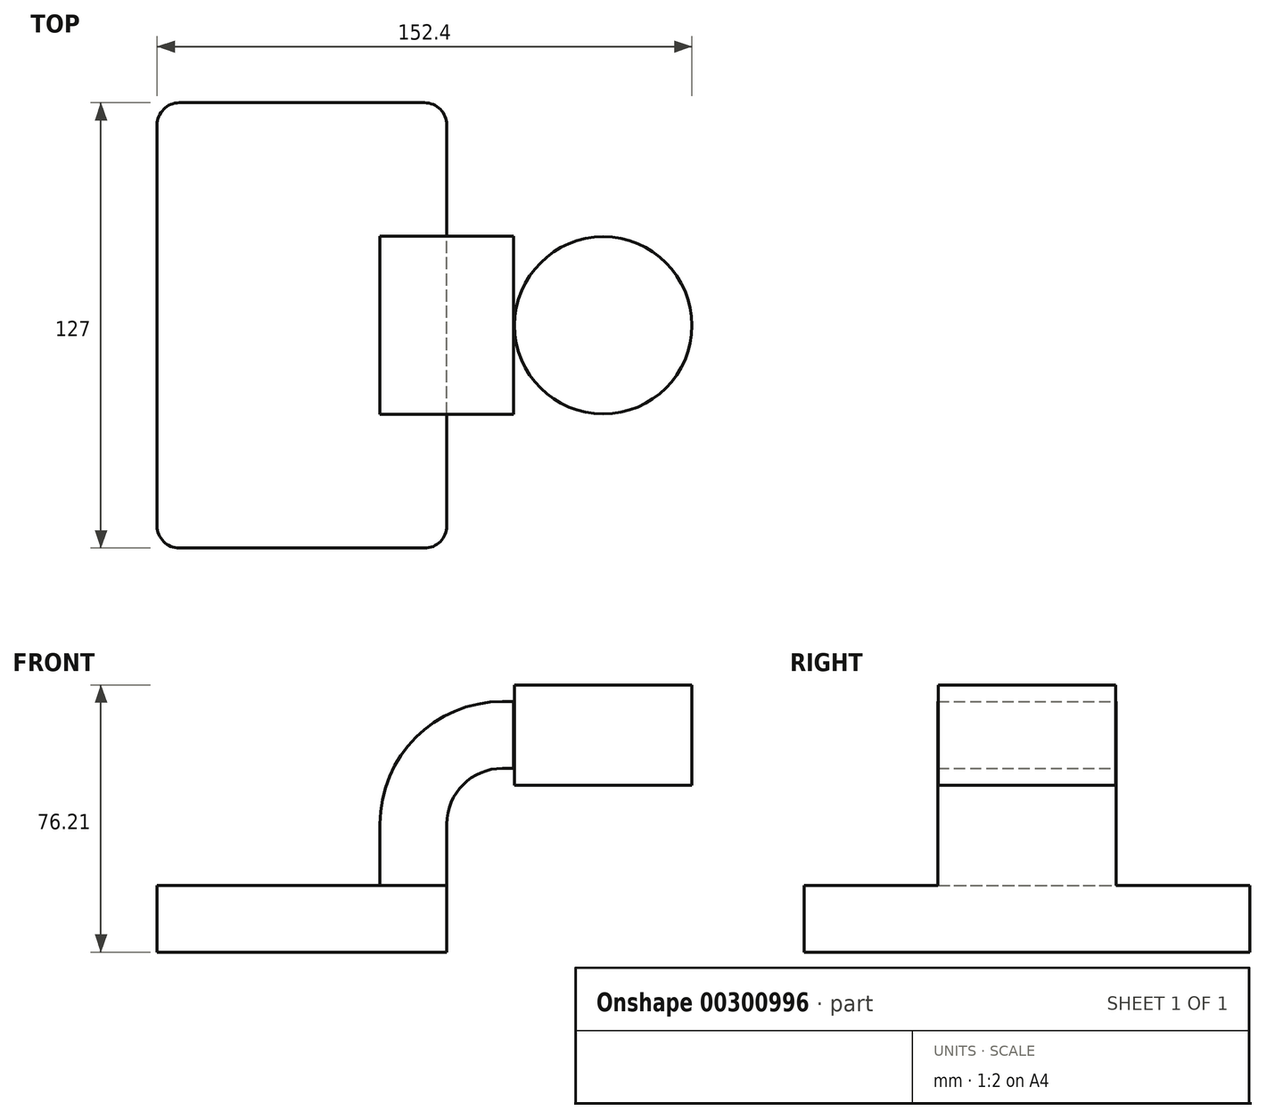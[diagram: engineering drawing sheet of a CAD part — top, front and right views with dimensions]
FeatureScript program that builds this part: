
annotation { "Feature Type Name" : "Feature", "Feature Type Description" : "" }
export const myFeature = defineFeature(function(context is Context, id is Id, definition is map)
    precondition{}
    {
        {
            var Q0;
            Q0=qCreatedBy(makeId("Front.planeOp"),FACE);
            var sketch = newSketch(context, id + "F0", { "sketchPlane" : qUnion([Q0])});
            skLineSegment(sketch, "E0.bottom", {"start": v(-41.28, 9.52) * mm, "end": v(41.27, 9.53) * mm});
            skLineSegment(sketch, "E0.top", {"start": v(-41.28, -9.53) * mm, "end": v(41.28, -9.53) * mm});
            skLineSegment(sketch, "E0.left", {"start": v(-41.28, 9.52) * mm, "end": v(-41.27, -9.53) * mm});
            skLineSegment(sketch, "E0.right", {"start": v(41.28, 9.53) * mm, "end": v(41.28, -9.52) * mm});
            skPoint(sketch, "E0.middle", {"position": v(0, 0) * mm});
            skLineSegment(sketch, "E1.bottom", {"start": v(60.32, 66.68) * mm, "end": v(111.12, 66.68) * mm});
            skLineSegment(sketch, "E1.top", {"start": v(60.32, 38.1) * mm, "end": v(111.12, 38.1) * mm});
            skLineSegment(sketch, "E1.left", {"start": v(60.32, 66.68) * mm, "end": v(60.32, 38.1) * mm});
            skLineSegment(sketch, "E1.right", {"start": v(111.12, 66.68) * mm, "end": v(111.12, 38.1) * mm});
            skPoint(sketch, "E1.middle", {"position": v(85.72, 52.39) * mm});
            skLineSegment(sketch, "E2", {"start": v(41.27, 9.53) * mm, "end": v(41.27, 27) * mm});
            skArc(sketch, "E3", {"start": v(41.27, 27) * mm, "mid": v(45.92, 38.23) * mm, "end": v(57.15, 42.88) * mm});
            skLineSegment(sketch, "E4", {"start": v(57.15, 42.88) * mm, "end": v(85.86, 42.88) * mm});
            skLineSegment(sketch, "E5.0", {"start": v(57.15, 61.93) * mm, "end": v(85.72, 61.93) * mm});
            skArc(sketch, "E5.1", {"start": v(22.22, 27) * mm, "mid": v(32.45, 51.7) * mm, "end": v(57.15, 61.93) * mm});
            skLineSegment(sketch, "E5.2", {"start": v(22.22, 9.53) * mm, "end": v(22.22, 27) * mm});
            skFitSpline(sketch, "E6", {"points": [v(-41.28, 9.52) * mm, v(57.15, 61.93) * mm], "startDerivative": vector(1, 104.21) * mm, "endDerivative": vector(115.49, -5.89) * mm});
            skLineSegment(sketch, "E7", {"start": v(85.86, 38.1) * mm, "end": v(85.86, 66.68) * mm});
            skLineSegment(sketch, "E8", {"start": v(60.32, 61.93) * mm, "end": v(60.32, 42.88) * mm});
            skLineSegment(sketch, "E9", {"start": v(60.32, 42.88) * mm, "end": v(85.86, 42.88) * mm});
            skLineSegment(sketch, "E10", {"start": v(85.72, 61.93) * mm, "end": v(85.86, 66.68) * mm});
            skLineSegment(sketch, "E11", {"start": v(60.32, 61.93) * mm, "end": v(60.32, 66.68) * mm});
            skSolve(sketch);
        }
        {
            var Q0;
            Q0=makeQuery(id+"F0.imprint","IMPRINT",FACE,{"disambiguationData":[TD([[makeQuery(id+"F0.imprint","IMPRINT",EDGE,{"derivedFrom":sQuery(id+"F0.wireOp",EDGE,"E0.top")}),1.0]])]});
            extrude(context, id + "F1", {"entities" : qUnion([Q0]), "endBound" : BoundingType.SYMMETRIC, "depth" : 127 * mm});
        }
        {
            var Q0;
            {var subQ1=sQuery(id+"F0.wireOp",EDGE,"E2");Q0=makeQuery(id+"F0.imprint","IMPRINT",FACE,{"disambiguationData":[TD([[makeQuery(id+"F0.imprint","IMPRINT",EDGE,{"derivedFrom":subQ1}),1.0]])]});}
            var Q1;
            {var subQ1=sQuery(id+"F0.wireOp",EDGE,"E8");Q1=makeQuery(id+"F0.imprint","IMPRINT",FACE,{"disambiguationData":[TD([[makeQuery(id+"F0.imprint","IMPRINT",EDGE,{"derivedFrom":subQ1}),1.0]])]});}
            extrude(context, id + "F2", {"entities" : qUnion([Q0, Q1]), "operationType" : NewBodyOperationType.ADD, "endBound" : BoundingType.SYMMETRIC, "depth" : 50.8 * mm});
        }
        {
            var Q0;
            Q0=makeQuery(id+"F0.imprint","IMPRINT",FACE,{"disambiguationData":[TD([[makeQuery(id+"F0.imprint","IMPRINT",EDGE,{"derivedFrom":sQuery(id+"F0.wireOp",EDGE,"E5.1")}),1.0]])]});
            extrude(context, id + "F3", {"entities" : qUnion([Q0]), "operationType" : NewBodyOperationType.ADD, "endBound" : BoundingType.SYMMETRIC, "depth" : 15.88 * mm});
        }
        {
            var Q0;
            {var subQ0=sQuery(id+"F0.wireOp",EDGE,"E1.right");Q0=makeQuery(id+"F0.imprint","IMPRINT",FACE,{"disambiguationData":[TD([[makeQuery(id+"F0.imprint","IMPRINT",EDGE,{"derivedFrom":subQ0}),-1.0]])]});}
            var Q1;
            Q1=sQuery(id+"F0.wireOp",EDGE,"E7");
            revolve(context, id + "F4", {"entities" : qUnion([Q0]), "axis" : qUnion([Q1]), "revolveType" : RevolveType.FULL});
        }
        {
            var Q0;
            Q0=makeQuery(id+"F1.opExtrude","CAP_EDGE",EDGE,{"disambiguationData":[OSD([sQuery(id+"F0.wireOp",EDGE,"E0.left")])],"isStart":false});
            var Q1;
            Q1=makeQuery(id+"F1.opExtrude","CAP_EDGE",EDGE,{"disambiguationData":[OSD([sQuery(id+"F0.wireOp",EDGE,"E0.right")])],"isStart":false});
            var Q2;
            Q2=makeQuery(id+"F1.opExtrude","CAP_EDGE",EDGE,{"disambiguationData":[OSD([sQuery(id+"F0.wireOp",EDGE,"E0.right")])],"isStart":true});
            var Q3;
            Q3=makeQuery(id+"F1.opExtrude","CAP_EDGE",EDGE,{"disambiguationData":[OSD([sQuery(id+"F0.wireOp",EDGE,"E0.left")])],"isStart":true});
            fillet(context, id + "F5", {"entities" : qUnion([Q0, Q1, Q2, Q3]), "radius" : 6.35 * mm, "tangentPropagation" : true, "allowEdgeOverflow" : false});
        }
    });
